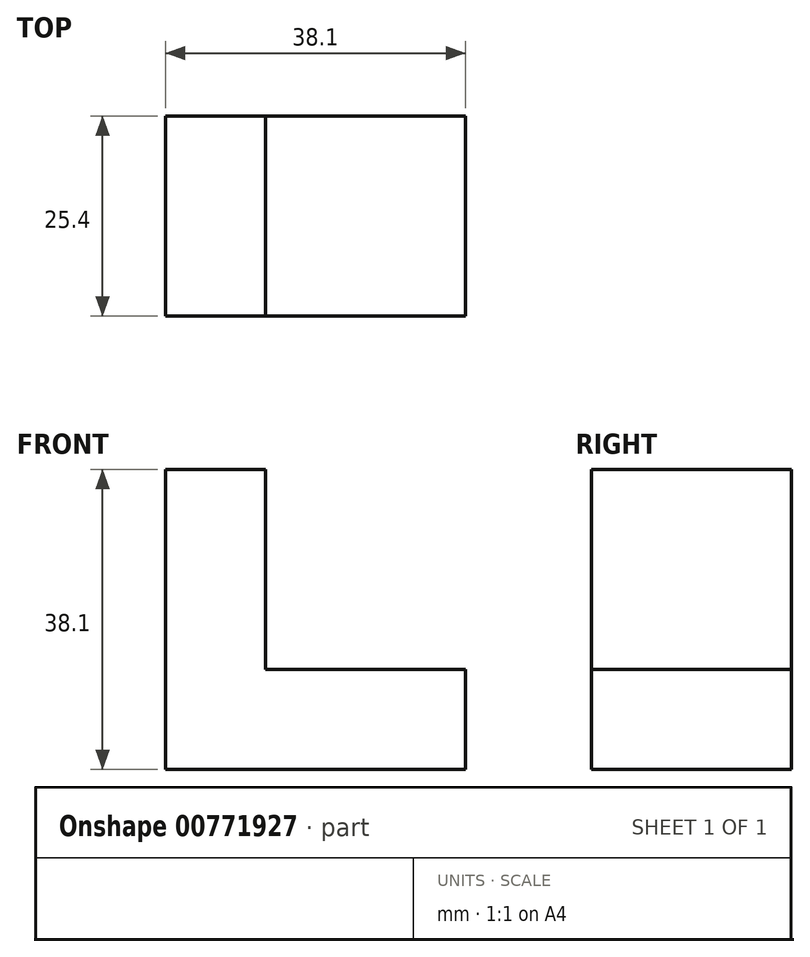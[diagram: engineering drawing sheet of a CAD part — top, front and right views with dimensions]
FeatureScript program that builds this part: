
annotation { "Feature Type Name" : "Feature", "Feature Type Description" : "" }
export const myFeature = defineFeature(function(context is Context, id is Id, definition is map)
    precondition{}
    {
        {
            var Q0;
            Q0=qCreatedBy(makeId("Front.planeOp"),FACE);
            var sketch = newSketch(context, id + "F0", { "sketchPlane" : qUnion([Q0])});
            skLineSegment(sketch, "E0", {"start": v(0, 0) * mm, "end": v(25.4, 0) * mm});
            skLineSegment(sketch, "E1", {"start": v(25.4, 0) * mm, "end": v(25.4, 12.7) * mm});
            skLineSegment(sketch, "E2", {"start": v(25.4, 12.7) * mm, "end": v(0, 12.7) * mm});
            skLineSegment(sketch, "E3", {"start": v(0, 0) * mm, "end": v(-12.7, 0) * mm});
            skLineSegment(sketch, "E4", {"start": v(-12.7, 0) * mm, "end": v(-12.7, 38.1) * mm});
            skLineSegment(sketch, "E5", {"start": v(-12.7, 38.1) * mm, "end": v(0, 38.1) * mm});
            skLineSegment(sketch, "E6", {"start": v(0, 38.1) * mm, "end": v(0, 12.7) * mm});
            skSolve(sketch);
        }
        {
            var Q0;
            Q0=makeQuery(id+"F0.imprint","IMPRINT",FACE,{"disambiguationData":[TD([[makeQuery(id+"F0.imprint","IMPRINT",EDGE,{"derivedFrom":sQuery(id+"F0.wireOp",EDGE,"E0")}),1.0]])]});
            extrude(context, id + "F1", {"entities" : qUnion([Q0]), "depth" : 25.4 * mm, "offsetDistance" : 25.4 * mm});
        }
    });
